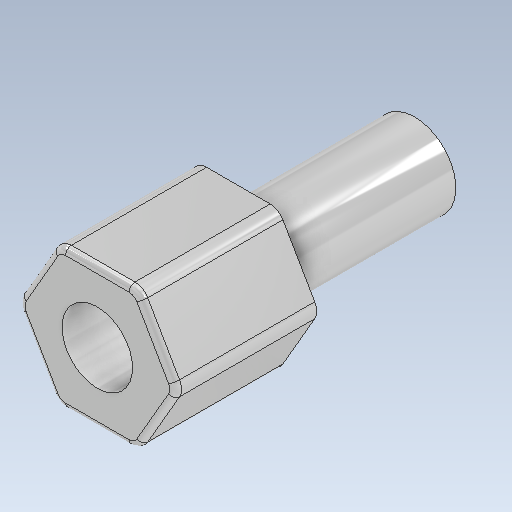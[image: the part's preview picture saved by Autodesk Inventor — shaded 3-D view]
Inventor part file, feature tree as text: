
AUTODESK INVENTOR PART (.ipt)
format: ipt  version: 2021 (Build 250183000, 183)  size: 168,960 bytes
history: native  units: mm
features: extrude x3, sketch x3, fillet x2
ambient origin geometry x8: Origin, YZ Plane, XZ Plane, XY Plane, X Axis, Y Axis, Z Axis, Center Point
bodies: Solid1 (feature_tree)
feature tree (8):
  extrude  "Extrusion1"  Depth=4.8mm TaperAngle=0.0deg
  extrude  "Extrusion2"  Depth=6.0mm TaperAngle=0.0deg
  extrude  "Extrusion3"  Depth=4.0mm TaperAngle=0.0deg
  fillet  "Fillet1"  Radius=0.5mm
  fillet  "Fillet2"  Radius=0.2mm
  sketch  "Sketch1"  dims[d0=4.75mm d1=4.8mm d2=0.0mm]
  sketch  "Sketch2"  dims[d3=2.8mm d4=6.0mm d5=0.0mm]
  sketch  "Sketch3"  dims[d6=2.4mm d7=4.0mm d8=0.0mm d9=0.5mm d10=0.2mm]
